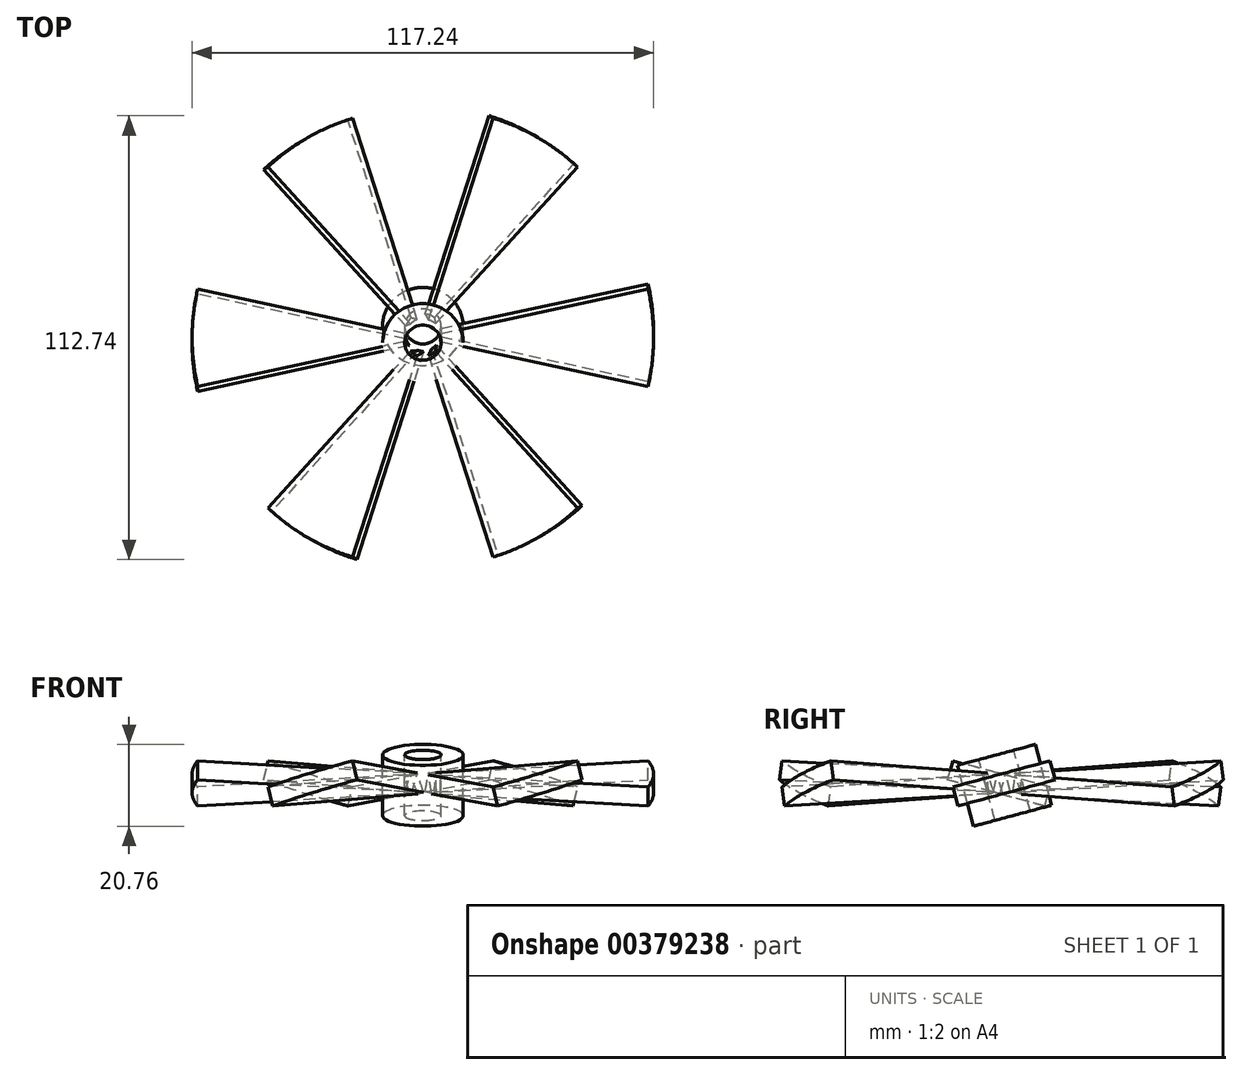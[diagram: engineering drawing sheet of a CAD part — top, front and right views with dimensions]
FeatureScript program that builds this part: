
annotation { "Feature Type Name" : "Feature", "Feature Type Description" : "" }
export const myFeature = defineFeature(function(context is Context, id is Id, definition is map)
    precondition{}
    {
        {
            var Q0;
            Q0=qCreatedBy(makeId("Top.planeOp"),FACE);
            var sketch = newSketch(context, id + "F0", { "sketchPlane" : qUnion([Q0])});
            skLineSegment(sketch, "E0", {"start": v(0, 0) * mm, "end": v(57.2, 12.81) * mm});
            skLineSegment(sketch, "E1", {"start": v(0, 0) * mm, "end": v(68.72, 0) * mm, "construction": true});
            skLineSegment(sketch, "E2.MirrorCS", {"start": v(0, 0) * mm, "end": v(57.2, -12.81) * mm});
            skArc(sketch, "E3", {"start": v(57.2, 12.81) * mm, "mid": v(58.62, 0) * mm, "end": v(57.2, -12.81) * mm});
            skSolve(sketch);
        }
        {
            var Q0;
            Q0=makeQuery(id+"F0.imprint","IMPRINT",FACE,{"disambiguationData":[TD([[makeQuery(id+"F0.imprint","IMPRINT",EDGE,{"derivedFrom":sQuery(id+"F0.wireOp",EDGE,"E0")}),-1.0]])]});
            extrude(context, id + "F1", {"entities" : qUnion([Q0]), "oppositeDirection" : true, "depth" : 5 * mm});
        }
        {
            var Q0;
            Q0=qCreatedBy(makeId("Top.planeOp"),FACE);
            var sketch = newSketch(context, id + "F2", { "sketchPlane" : qUnion([Q0])});
            skLineSegment(sketch, "E4", {"start": v(0, 0) * mm, "end": v(59.8, 0) * mm, "construction": true});
            skSolve(sketch);
        }
        {
            var Q0;
            Q0=makeQuery(id+"F1.opExtrude","SWEPT_BODY",BODY,{"disambiguationData":[OSD([sQuery(id+"F0.wireOp",EDGE,"E0"),sQuery(id+"F0.wireOp",EDGE,"E2.MirrorCS"),sQuery(id+"F0.wireOp",EDGE,"E3")])]});
            var Q1;
            Q1=sQuery(id+"F2.wireOp",EDGE,"E4");
            transform(context, id + "F3", {"entities" : qUnion([Q0]), "transformType" : TransformType.ROTATION, "transformAxis" : qUnion([Q1]), "angle" : 15 * degree, "makeCopy" : false});
        }
        {
            var Q0;
            Q0=qCreatedBy(makeId("Front.planeOp"),FACE);
            var sketch = newSketch(context, id + "F4", { "sketchPlane" : qUnion([Q0])});
            skLineSegment(sketch, "E5", {"start": v(0, 23.53) * mm, "end": v(0, -34.11) * mm, "construction": true});
            skSolve(sketch);
        }
        {
            var Q0;
            Q0=makeQuery(id+"F1.opExtrude","SWEPT_BODY",BODY,{"disambiguationData":[OSD([sQuery(id+"F0.wireOp",EDGE,"E0"),sQuery(id+"F0.wireOp",EDGE,"E2.MirrorCS"),sQuery(id+"F0.wireOp",EDGE,"E3")])]});
            var Q1;
            Q1=sQuery(id+"F4.wireOp",EDGE,"E5");
            circularPattern(context, id + "F5", {"entities" : qUnion([Q0]), "axis" : qUnion([Q1]), "angle" : 360 * degree, "instanceCount" : 6, "equalSpace" : true});
        }
        {
            var Q0;
            Q0=qCreatedBy(makeId("Top.planeOp"),FACE);
            var sketch = newSketch(context, id + "F6", { "sketchPlane" : qUnion([Q0])});
            skCircle(sketch, "E6", {"center": v(0, 0) * mm, "radius": 10.26 * mm});
            skSolve(sketch);
        }
        {
            var Q0;
            Q0 = qSketchRegion(id + "F6", true);
            var Q1;
            Q1=makeQuery(id+"F5.opPattern","COPY",FACE,{"derivedFrom":makeQuery(id+"F1.opExtrude","CAP_FACE",FACE,{"disambiguationData":[OSD([sQuery(id+"F0.wireOp",EDGE,"E0"),sQuery(id+"F0.wireOp",EDGE,"E2.MirrorCS"),sQuery(id+"F0.wireOp",EDGE,"E3")])],"isStart":false}),"instanceName":"5"});
            var Q2;
            Q2=makeQuery(id+"F5.opPattern","COPY",VERTEX,{"derivedFrom":makeQuery(id+"F1.opExtrude","CAP_VERTEX",VERTEX,{"disambiguationData":[OSD([sQuery(id+"F0.wireOp",EDGE,"E0"),sQuery(id+"F0.wireOp",EDGE,"E2.MirrorCS")])],"isStart":false}),"instanceName":"1"});
            extrude(context, id + "F7", {"entities" : qUnion([Q0]), "oppositeDirection" : true, "endBoundEntityFace" : qUnion([Q1]), "endBoundEntityVertex" : qUnion([Q2]), "depth" : 11 * mm, "hasSecondDirection" : true, "secondDirectionOppositeDirection" : false, "secondDirectionDepth" : 5 * mm});
        }
        {
            var Q0;
            Q0=makeQuery(id+"F7.opExtrude","SWEPT_BODY",BODY,{"disambiguationData":[OSD([sQuery(id+"F6.wireOp",EDGE,"E6")])]});
            var Q1;
            Q1=sQuery(id+"F2.wireOp",EDGE,"E4");
            transform(context, id + "F8", {"entities" : qUnion([Q0]), "transformType" : TransformType.ROTATION, "transformAxis" : qUnion([Q1]), "angle" : 15 * degree, "makeCopy" : false});
        }
        {
            var Q0;
            Q0=makeQuery(id+"F7.opExtrude","CAP_FACE",FACE,{"disambiguationData":[OSD([sQuery(id+"F6.wireOp",EDGE,"E6")])],"isStart":true});
            var sketch = newSketch(context, id + "F9", { "sketchPlane" : qUnion([Q0])});
            skCircle(sketch, "E7", {"center": v(0, 0) * mm, "radius": 4.62 * mm});
            skSolve(sketch);
        }
        {
            var Q0;
            Q0=makeQuery(id+"F9.imprint","IMPRINT",FACE,{"disambiguationData":[TD([[makeQuery(id+"F9.imprint","IMPRINT",EDGE,{"derivedFrom":sQuery(id+"F9.wireOp",EDGE,"E7")}),1.0]])]});
            extrude(context, id + "F10", {"entities" : qUnion([Q0]), "oppositeDirection" : true, "depth" : 25 * mm, "hasSecondDirection" : true, "secondDirectionOppositeDirection" : false, "secondDirectionDepth" : 25 * mm});
        }
        {
            var Q0;
            Q0=makeQuery(id+"F10.opExtrude","SWEPT_BODY",BODY,{"disambiguationData":[OSD([sQuery(id+"F9.wireOp",EDGE,"E7")])]});
            var Q1;
            Q1=makeQuery(id+"F7.opExtrude","SWEPT_BODY",BODY,{"disambiguationData":[OSD([sQuery(id+"F6.wireOp",EDGE,"E6")])]});
            var Q2;
            Q2=makeQuery(id+"F5.opPattern","COPY",BODY,{"derivedFrom":makeQuery(id+"F1.opExtrude","SWEPT_BODY",BODY,{"disambiguationData":[OSD([sQuery(id+"F0.wireOp",EDGE,"E0"),sQuery(id+"F0.wireOp",EDGE,"E2.MirrorCS"),sQuery(id+"F0.wireOp",EDGE,"E3")])]}),"instanceName":"4"});
            var Q3;
            Q3=makeQuery(id+"F5.opPattern","COPY",BODY,{"derivedFrom":makeQuery(id+"F1.opExtrude","SWEPT_BODY",BODY,{"disambiguationData":[OSD([sQuery(id+"F0.wireOp",EDGE,"E0"),sQuery(id+"F0.wireOp",EDGE,"E2.MirrorCS"),sQuery(id+"F0.wireOp",EDGE,"E3")])]}),"instanceName":"3"});
            var Q4;
            Q4=makeQuery(id+"F5.opPattern","COPY",BODY,{"derivedFrom":makeQuery(id+"F1.opExtrude","SWEPT_BODY",BODY,{"disambiguationData":[OSD([sQuery(id+"F0.wireOp",EDGE,"E0"),sQuery(id+"F0.wireOp",EDGE,"E2.MirrorCS"),sQuery(id+"F0.wireOp",EDGE,"E3")])]}),"instanceName":"2"});
            var Q5;
            Q5=makeQuery(id+"F5.opPattern","COPY",BODY,{"derivedFrom":makeQuery(id+"F1.opExtrude","SWEPT_BODY",BODY,{"disambiguationData":[OSD([sQuery(id+"F0.wireOp",EDGE,"E0"),sQuery(id+"F0.wireOp",EDGE,"E2.MirrorCS"),sQuery(id+"F0.wireOp",EDGE,"E3")])]}),"instanceName":"1"});
            var Q6;
            Q6=makeQuery(id+"F1.opExtrude","SWEPT_BODY",BODY,{"disambiguationData":[OSD([sQuery(id+"F0.wireOp",EDGE,"E0"),sQuery(id+"F0.wireOp",EDGE,"E2.MirrorCS"),sQuery(id+"F0.wireOp",EDGE,"E3")])]});
            var Q7;
            Q7=makeQuery(id+"F5.opPattern","COPY",BODY,{"derivedFrom":makeQuery(id+"F1.opExtrude","SWEPT_BODY",BODY,{"disambiguationData":[OSD([sQuery(id+"F0.wireOp",EDGE,"E0"),sQuery(id+"F0.wireOp",EDGE,"E2.MirrorCS"),sQuery(id+"F0.wireOp",EDGE,"E3")])]}),"instanceName":"5"});
            booleanBodies(context, id + "F11", {"operationType" : BooleanOperationType.SUBTRACTION, "tools" : qUnion([Q0]), "targets" : qUnion([Q1, Q2, Q3, Q4, Q5, Q6, Q7])});
        }
    });
